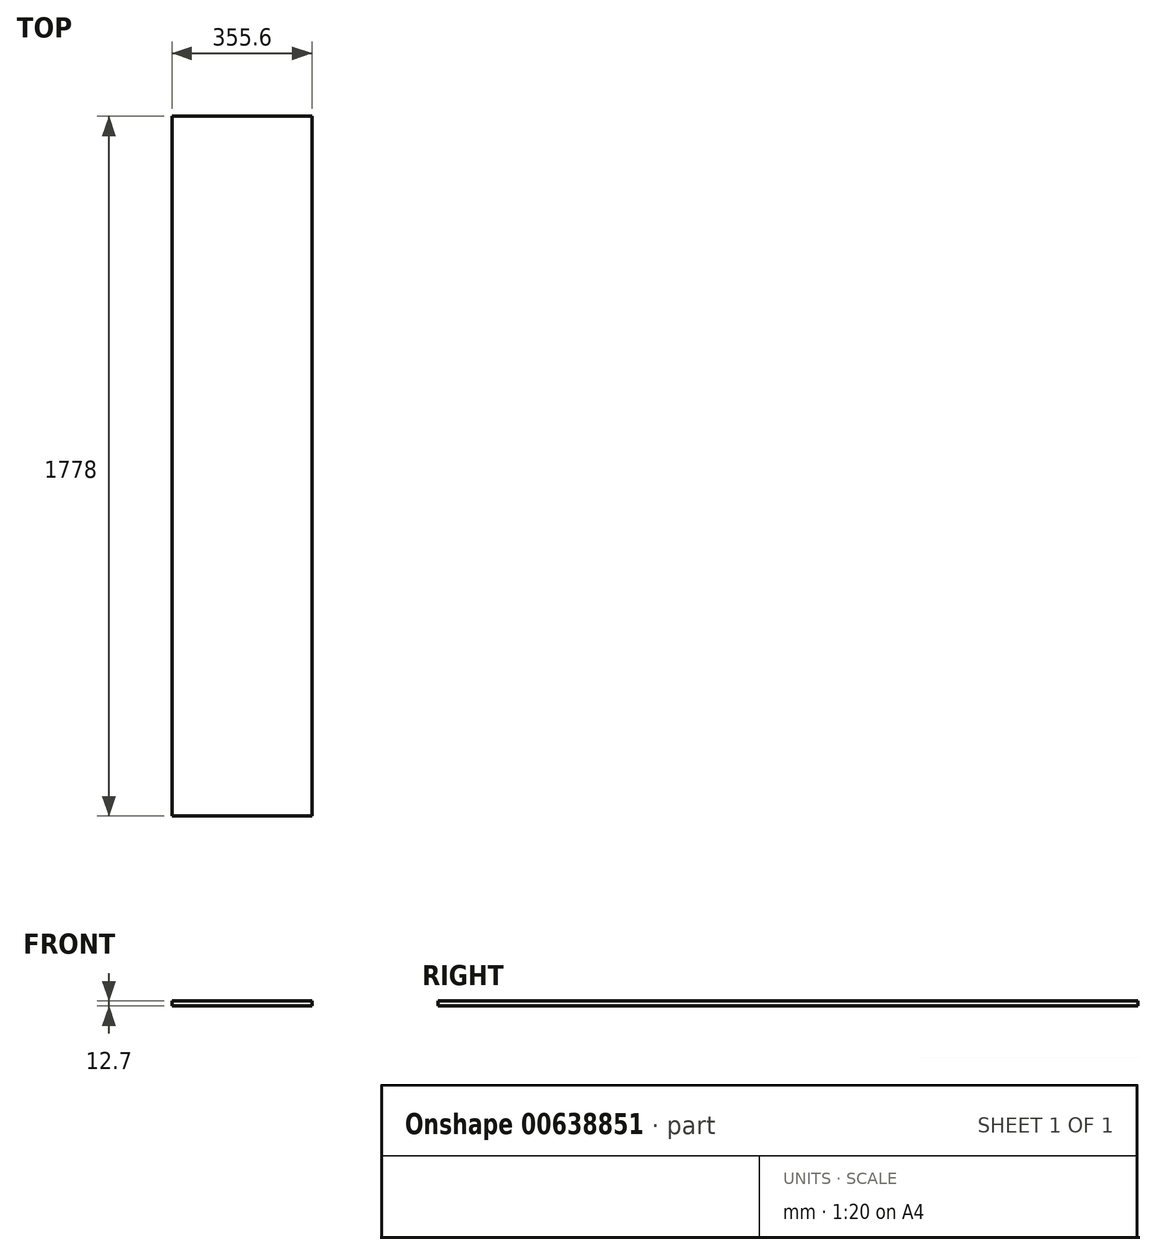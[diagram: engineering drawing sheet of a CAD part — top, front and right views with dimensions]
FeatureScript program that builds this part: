
annotation { "Feature Type Name" : "Feature", "Feature Type Description" : "" }
export const myFeature = defineFeature(function(context is Context, id is Id, definition is map)
    precondition{}
    {
        {
            var Q0;
            Q0=qCreatedBy(makeId("Top.planeOp"),FACE);
            var sketch = newSketch(context, id + "F0", { "sketchPlane" : qUnion([Q0])});
            skLineSegment(sketch, "E0.bottom", {"start": v(177.8, 889) * mm, "end": v(-177.8, 889) * mm});
            skLineSegment(sketch, "E0.top", {"start": v(177.8, -889) * mm, "end": v(-177.8, -889) * mm});
            skLineSegment(sketch, "E0.left", {"start": v(177.8, 889) * mm, "end": v(177.8, -889) * mm});
            skLineSegment(sketch, "E0.right", {"start": v(-177.8, 889) * mm, "end": v(-177.8, -889) * mm});
            skPoint(sketch, "E0.middle", {"position": v(0, 0) * mm});
            skSolve(sketch);
        }
        {
            var Q0;
            Q0=makeQuery(id+"F0.imprint","IMPRINT",FACE,{"disambiguationData":[TD([[makeQuery(id+"F0.imprint","IMPRINT",EDGE,{"derivedFrom":sQuery(id+"F0.wireOp",EDGE,"E0.bottom")}),1.0]])]});
            extrude(context, id + "F1", {"entities" : qUnion([Q0]), "depth" : 12.7 * mm, "offsetDistance" : 25.4 * mm});
        }
    });
